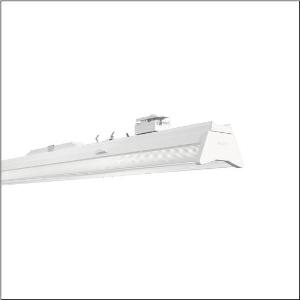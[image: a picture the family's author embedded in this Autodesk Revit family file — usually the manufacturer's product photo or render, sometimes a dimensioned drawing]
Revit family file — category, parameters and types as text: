
# Revit family: licross_21_performance_mo_52td16vn465g
name_source: partatom
category: Lighting Fixtures
units: mm (PartAtom-declared; Revit-internal decimal feet)

## family parameters
Cut with Voids When Loaded = No
Host = Face
Light Source = No
Part Type = Normal
Room Calculation Point = No
Round Connector Dimension = Use Diameter
Shared = No

## types (1)
- --- (1 x LED, 6500 lm, 36.1 W, 4000K)
    Apparent Load = 36 VA
    CIE Flux Codes = 66 88 96 79 100
    Color Rendering = 80
    Color Temperature = 4000K
    Default Elevation = 1800 mm
    Description = Licross 21 Performance MO, luminaire insert, of sheet steel, galvanised, coil coated, white, length: 1.500mm, width: 120mm, height: 123mm, LED rated luminous flux: 6.500lm, light colour: 840, SDCM (Standard Deviation of Colour Matching)MacAdam ≤ 3 SDCM (initial), control gear: DALI 2, CLO, with plug, 5-pole, with phase selection, mains connection: 220..240V, AC, 50/60Hz, start of lifetime: 36W, end of service life: 43W, internal wiring halogen-free, primary light control with lens, of plastic, primary optical cover: cover, of PMMA, light emission: direct/indirect distribution, primary light characteristic: symmetric, protection rating (complete): IP54, insulation class (complete): insulation class I (protective earthing), certification: CE, ENEC, VDE, UKCA, protection symbol: D if used in an environment with non-conductive dust loads with corresponding accessories, impact resistance: IK06, permissible ambient temperature for indoor applications: -25..+45°C, corresponds to IFS (International Featured Standards) requirements for safety and quality in the food industry, reducing of maximum allowable ambient temperature of 5°C with ceiling mounting, LABS conformity tested according to VDMA 24364:2018-05, The light source and the operating device comply with the requirements of the Ecodesign Regulation (EU) 2019/2020 and are replaceable in accordance with this regulation, packaging unit: 1 piece
    Height = 114 mm
    Lamp = 1 x LED
    Lamp Light Flux = 6500 lm
    Lamp Power = 36.1 W
    Lamp count = 1
    Length = 1500 mm
    Luminous efficacy = 180 lm/W
    Manufacturer = Siteco
    ModVariant = No
    Model = 52TD16VN465G
    Mounting Place = Ceiling
    Mounting Type = Pendant
    Number of Poles = 1
    OnlyDefault = Yes
    Power Factor = 1
    Product Name = Licross 21 Performance MO
    Product group = luminaire insert | ceiling pendant
    ProductGroupID = 901
    Protection Class = Protection class I
    Protection Degree = IP 54
    RLX_Detail_Level = 1
    RLX_Emergency_Light_Flux = 0 lm
    RLX_Emergency_Type = 0
    RLX_Emergency_Type_DB = No
    RlxData = <blob elided: 34373 chars, md5=089997cc>
    Socket = socket
    Standby Power = 0 W
    System Light Flux = 6500 lm
    System Power = 36 W
    Type Comments = factory setting: luminous flux: 100 % | dim-lin: 254 | 242 mA
    Type Image = l_1256138.jpg
    URL = http://relux.com
    VarID = @adj_089585
    Voltage = 0 V
    Weight = 0.00 kg
    Width = 120 mm

## geometry (parser evidence)
native form markers: Blend x4, Sweep x12
no freeform markers — native parametric forms only
